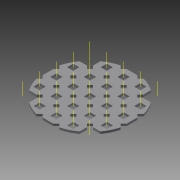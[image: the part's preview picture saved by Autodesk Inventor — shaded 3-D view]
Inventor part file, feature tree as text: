
AUTODESK INVENTOR PART (.ipt)
format: ipt  version: 2015 SP1 (Build 190203100, 203)  size: 1,211,392 bytes
history: native  units: in
note: dims shown in document units (in); Inventor stores cm internally (conversion verified against a paired STEP export)
features: other x34, extrude x4, sketch x2, pattern_linear x1, pattern_circular x1, imported_body x1
ambient origin geometry x8: Origin, YZ Plane, XZ Plane, XY Plane, X Axis, Y Axis, Z Axis, Center Point
bodies: Body1 (feature_tree)
feature tree (43):
  other  "Diamond-Pattern"
  other  "Plate"
  extrude  "length cut"  TaperAngle=0.0deg  [1 undecoded]
  extrude  "width cut"  Depth=0.5in
  other  "constraint axis"
  pattern_linear  "constraint axes"  Spacing1=-2.5in  [1 undecoded]
  other  "front plane"
  other  "right plane"
  extrude  "Extrusion4"  [1 undecoded]
  pattern_circular  "Circular Pattern1"  [2 undecoded]
  extrude  "Extrusion5"  TaperAngle=0.0deg  [1 undecoded]
  imported_body  "Base1"
  other  "length profile"
  other  "width profile"
  other  "Work Point1"
  other  "Work Axis36"
  other  "Work Axis40"
  other  "Work Axis41"
  other  "Work Axis42"
  other  "Work Axis43"
  other  "back plane"
  other  "left plane"
  other  "Work Axis120"
  other  "Work Axis121"
  other  "Work Axis122"
  other  "Work Axis123"
  other  "Work Axis170"
  other  "Work Axis171"
  other  "Work Axis172"
  other  "Work Axis173"
  other  "Work Axis174"
  other  "Work Axis175"
  other  "Work Axis176"
  other  "Work Axis177"
  other  "Work Axis178"
  other  "Work Axis179"
  other  "Work Axis180"
  other  "Work Axis181"
  other  "Work Axis182"
  other  "Work Axis183"
  other  "Work Axis184"
  sketch  "Sketch3"  dims[d1=0.0in d5=0.0in]
  sketch  "Sketch4"  dims[d8=0.5in d11=0.5in d12=-2.5in d13=-2.5in d14=0.0in d15=0.0in d16=0.0in d17=0.0in d18=0.0in d19=0.0in d21=0.0in d22=0.0in d23=0.0in d24=1.5748in d25=2.4737in d27=0.05in d28=0.0in d29=0.0in]
note: 6 required parameter values undecoded (feature->parameter linkage not recoverable at this tier; creation-order binding heuristic only, values carry confidence <= 0.55)
